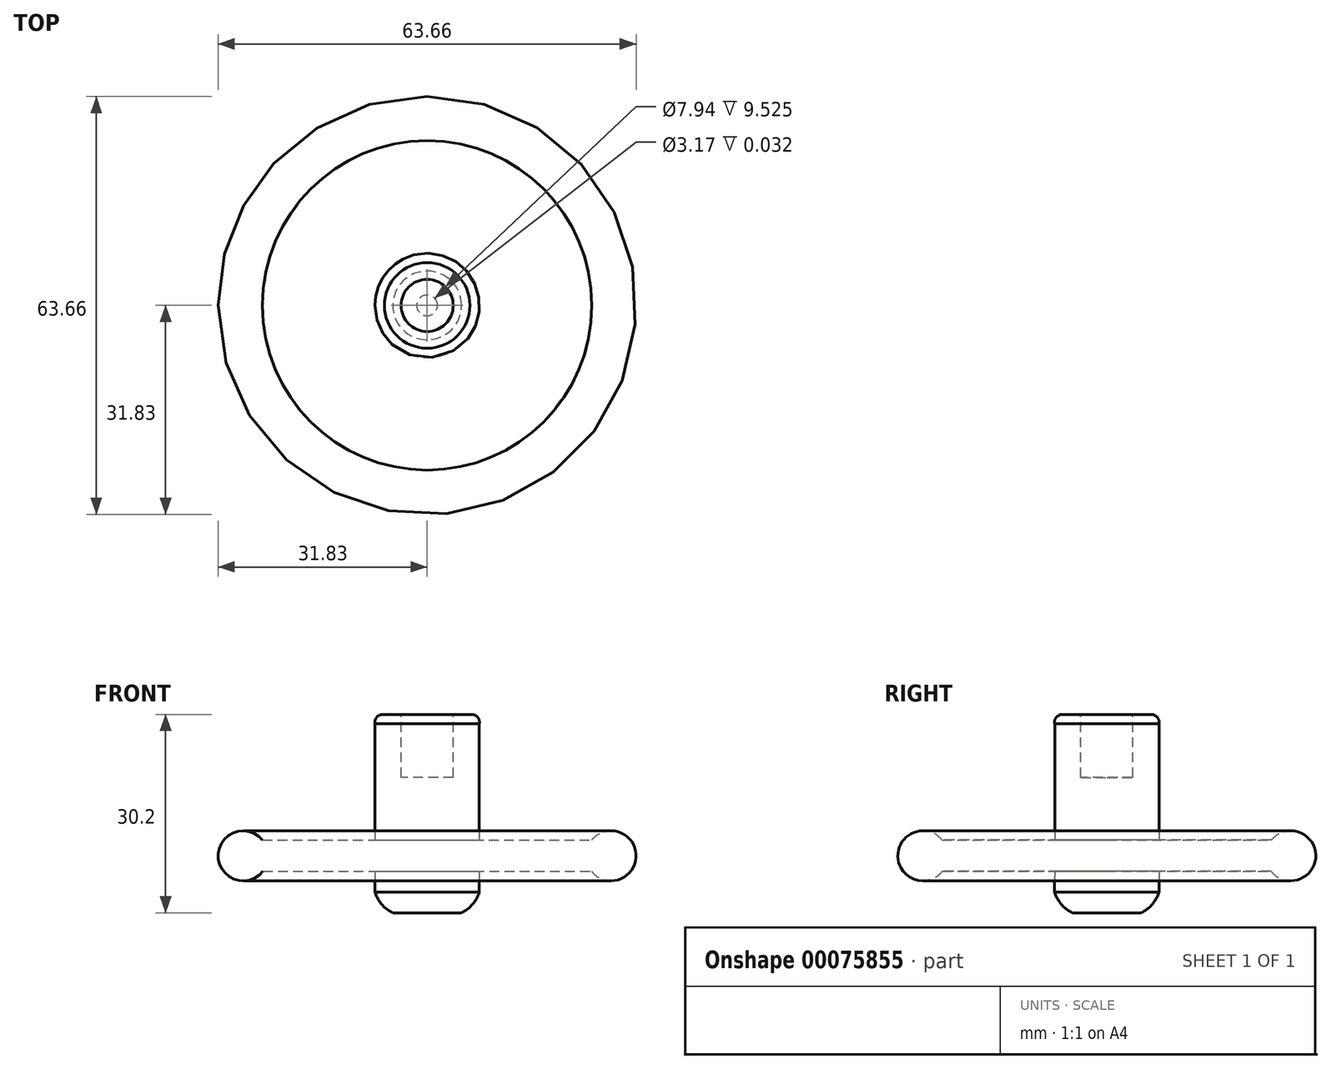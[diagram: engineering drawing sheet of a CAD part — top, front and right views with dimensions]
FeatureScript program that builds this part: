
annotation { "Feature Type Name" : "Feature", "Feature Type Description" : "" }
export const myFeature = defineFeature(function(context is Context, id is Id, definition is map)
    precondition{}
    {
        {
            var Q0;
            Q0=qCreatedBy(makeId("Front.planeOp"),FACE);
            var sketch = newSketch(context, id + "F0", { "sketchPlane" : qUnion([Q0])});
            skLineSegment(sketch, "E0", {"start": v(0, 0) * mm, "end": v(0, 30.16) * mm});
            skLineSegment(sketch, "E1", {"start": v(7.94, 11.11) * mm, "end": v(25.09, 11.11) * mm});
            skLineSegment(sketch, "E2", {"start": v(7.94, 6.35) * mm, "end": v(25.01, 6.35) * mm});
            skArc(sketch, "E3", {"start": v(25.01, 6.35) * mm, "mid": v(31.83, 8.62) * mm, "end": v(25.09, 11.11) * mm});
            skArc(sketch, "E4", {"start": v(5.23, 0) * mm, "mid": v(6.93, 1.3) * mm, "end": v(7.94, 3.17) * mm});
            skLineSegment(sketch, "E5", {"start": v(7.94, 3.17) * mm, "end": v(7.94, 6.35) * mm});
            skLineSegment(sketch, "E6", {"start": v(5.23, 0) * mm, "end": v(0, 0) * mm});
            skArc(sketch, "E7", {"start": v(7.94, 28.8) * mm, "mid": v(7.61, 29.88) * mm, "end": v(6.52, 30.16) * mm});
            skLineSegment(sketch, "E8", {"start": v(0, 30.16) * mm, "end": v(6.52, 30.16) * mm});
            skLineSegment(sketch, "E9", {"start": v(7.94, 28.8) * mm, "end": v(7.94, 11.11) * mm});
            skSolve(sketch);
        }
        {
            var Q0;
            Q0 = qSketchRegion(id + "F0", true);
            var Q1;
            Q1=sQuery(id+"F0.wireOp",EDGE,"E0");
            revolve(context, id + "F1", {"entities" : qUnion([Q0]), "axis" : qUnion([Q1]), "revolveType" : RevolveType.FULL});
        }
        {
            var Q0;
            Q0=makeQuery(id+"F1.opRevolve","SWEPT_FACE",FACE,{"disambiguationData":[OSD([sQuery(id+"F0.wireOp",EDGE,"E8")])]});
            var sketch = newSketch(context, id + "F2", { "sketchPlane" : qUnion([Q0])});
            skCircle(sketch, "E10", {"center": v(0, 0) * mm, "radius": 3.97 * mm});
            skSolve(sketch);
        }
        {
            var Q0;
            Q0 = qSketchRegion(id + "F2", true);
            extrude(context, id + "F3", {"entities" : qUnion([Q0]), "operationType" : NewBodyOperationType.REMOVE, "oppositeDirection" : true, "depth" : 9.52 * mm});
        }
        {
            var Q0;
            Q0=makeQuery(id+"F1.opRevolve","SWEPT_FACE",FACE,{"disambiguationData":[OSD([sQuery(id+"F0.wireOp",EDGE,"E6")])]});
            var sketch = newSketch(context, id + "F4", { "sketchPlane" : qUnion([Q0])});
            skCircle(sketch, "E11", {"center": v(0, 0) * mm, "radius": 1.59 * mm});
            skSolve(sketch);
        }
        {
            var Q0;
            Q0 = qSketchRegion(id + "F4", true);
            extrude(context, id + "F5", {"entities" : qUnion([Q0]), "operationType" : NewBodyOperationType.REMOVE, "oppositeDirection" : true, "depth" : 13 / 406.4 * mm});
        }
    });
